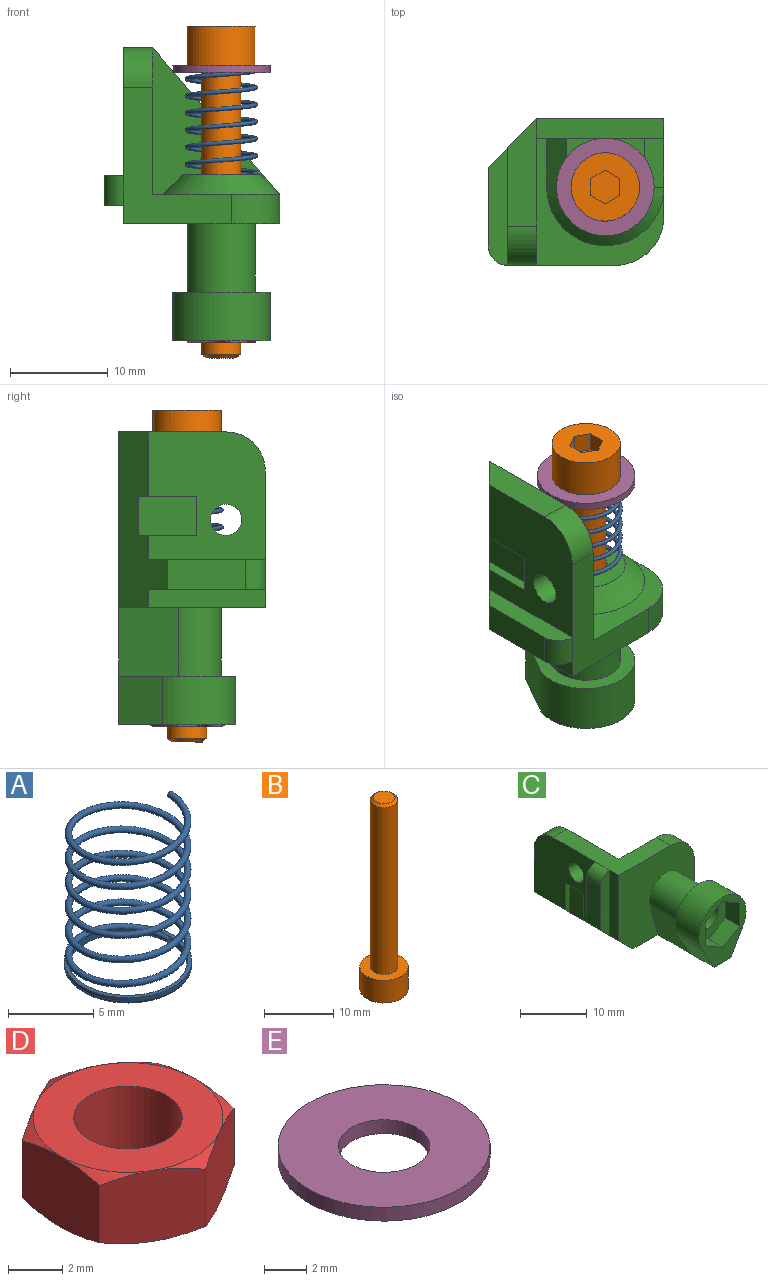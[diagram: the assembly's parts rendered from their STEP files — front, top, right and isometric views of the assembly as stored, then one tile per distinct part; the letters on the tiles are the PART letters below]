
ASSEMBLY  parts=5 mates=4
PART A: 8 faces, bbox 8.2x8.2x11.1 mm
  f0: bspline ~10.9x7.4mm, area 163.9mm2, adj f1,f2,f3,f4,f6
  f1: plane 0.46x0.26mm, normal (0,-1,0), area 0.1mm2, adj f0,f3
  f2: plane 0.46x0.46mm, normal (0,1,0), area 0.1mm2, adj f0
  f3: cylinder r=3.5mm len=7mm, axis (0,0,-1), area 9.7mm2, adj f0,f1,f4,f6,f7
  f4: cylinder r=3.5mm len=0.66mm, axis (0,0,-1), area 0mm2, adj f0,f3,f6
  f5: cylinder r=3.75mm len=7.5mm, axis (0,0,-1), area 5.9mm2, adj f6,f7
  f6: plane 7.61x7.61mm, normal (0,0,1), area 4.9mm2, adj f0,f3,f4,f5
  f7: torus R=3.5mm, axis (0,0,1), area 9mm2, adj f3,f5
PART B: 13 faces, bbox 7x7x34 mm
  f0: plane 7x7mm, normal (0,0,-1), area 30.7mm2, adj f2,f6,f7,f8,f9,f10,f11
  f1: plane 3.2x3.2mm, normal (0,0,1), area 8mm2, adj f5
  f2: cylinder r=3.5mm len=7mm, axis (0,0,-1), area 88mm2, adj f0,f3
  f3: plane 7x7mm, normal (0,0,1), area 25.9mm2, adj f2,f4
  f4: cylinder r=2mm len=29.6mm, axis (0,0,-1), area 372mm2, adj f3,f5
  f5: cone r=2mm half-angle=45deg, axis (0,0,-1), area 6.4mm2, adj f1,f4
  f6: plane 2x1.73mm, normal (-1,0,0), area 3.5mm2, adj f0,f7,f11,f12
  f7: plane 2x1.5mm, normal (-0.5,-0.87,0), area 3.5mm2, adj f0,f6,f8,f12
  f8: plane 2x1.5mm, normal (0.5,-0.87,0), area 3.5mm2, adj f0,f7,f9,f12
  f9: plane 2x1.73mm, normal (1,0,0), area 3.5mm2, adj f0,f8,f10,f12
  f10: plane 2x1.5mm, normal (0.5,0.87,0), area 3.5mm2, adj f0,f9,f11,f12
  f11: plane 2x1.5mm, normal (-0.5,0.87,0), area 3.5mm2, adj f0,f6,f10,f12
  f12: plane 3.46x3mm, normal (0,0,-1), area 7.8mm2, adj f6,f7,f8,f9,f10,f11
PART C: 43 faces, bbox 18x30x15 mm
  f0: plane 13.1x12mm, normal (-1,0,0), area 125.7mm2, adj f1,f8,f9,f16,f32,f34,f39,f40
  f1: plane 18x5mm, normal (-0.71,0,-0.71), area 79.2mm2, adj f0,f2,f3,f6,f8,f9,f10,f11
  f2: plane 8x3mm, normal (-1,0,0), area 24mm2, adj f1,f9,f10,f33
  f3: plane 30x13mm, normal (0,0,-1), area 178.5mm2, adj f1,f4,f6,f12,f13,f17,f18,f20
  f4: plane 12x10mm, normal (0,-1,0), area 44.4mm2, adj f3,f20,f21,f22,f26,f27,f28,f29
  f5: cylinder r=2.15mm len=14mm, axis (0,1,0), area 189.1mm2, adj f24,f25
  f6: plane 16x15mm, normal (0,-1,0), area 173.4mm2, adj f1,f3,f11,f12,f16,f17,f18,f19
  f7: plane 15x13mm, normal (0,0,1), area 77.5mm2, adj f13,f14,f15,f24,f36,f38
  f8: plane 11x3mm, normal (0,1,0), area 28.5mm2, adj f0,f1,f13,f14,f34
  f9: plane 12x2mm, normal (0,1,0), area 21.1mm2, adj f0,f1,f2,f33
  f10: plane 12x2mm, normal (0,-1,0), area 21.1mm2, adj f1,f2,f11,f33
  f11: plane 12x1.9mm, normal (-1,0,0), area 22.8mm2, adj f1,f6,f10,f16
  f12: plane 10x3mm, normal (1,0,0), area 30mm2, adj f3,f6,f13,f15,f35,f36
  f13: plane 15x13mm, normal (0.76,0.65,0), area 39.7mm2, adj f3,f7,f8,f12
  f14: plane 15x13mm, normal (1,0,0), area 183.5mm2, adj f7,f8,f15,f16,f32,f34
  f15: plane 13x13mm, normal (0,1,0), area 47.1mm2, adj f7,f12,f14,f16,f35,f37,f38
  f16: plane 14x11mm, normal (0,0,1), area 66mm2, adj f0,f6,f11,f14,f15,f33,f34,f35
  f17: plane 7x6.1mm, normal (-0.97,0,-0.26), area 44.2mm2, adj f3,f6,f19,f23
  f18: plane 7x6.1mm, normal (0.97,0,-0.26), area 44.2mm2, adj f3,f6,f19,f23
  f19: cylinder r=3.5mm len=7mm, axis (0,1,0), area 89.8mm2, adj f6,f17,f18,f23
  f20: plane 5x4.51mm, normal (-0.87,0,-0.5), area 26mm2, adj f3,f4,f22,f23
  f21: plane 5x4.51mm, normal (0.87,0,-0.5), area 26mm2, adj f3,f4,f22,f23
  f22: cylinder r=5mm len=10mm, axis (0,1,0), area 104.6mm2, adj f4,f20,f21,f23
  f23: plane 12x10mm, normal (0,1,0), area 33.8mm2, adj f17,f18,f19,f20,f21,f22
  f24: plane 9x8mm, normal (0,1,0), area 50.6mm2, adj f5,f7,f36,f37,f38
  f25: plane 8.43x7.3mm, normal (0,-1,0), area 31.6mm2, adj f5,f26,f27,f28,f29,f30,f31
  f26: plane 4.21x3mm, normal (-1,0,0), area 12.6mm2, adj f4,f25,f27,f31
  f27: plane 3.65x3mm, normal (-0.5,0,-0.87), area 12.6mm2, adj f4,f25,f26,f28
  f28: plane 3.65x3mm, normal (0.5,0,-0.87), area 12.6mm2, adj f4,f25,f27,f29
  f29: plane 4.21x3mm, normal (1,0,0), area 12.6mm2, adj f4,f25,f28,f30
  f30: plane 3.65x3mm, normal (0.5,0,0.87), area 12.6mm2, adj f4,f25,f29,f31
  f31: plane 3.65x3mm, normal (-0.5,0,0.87), area 12.6mm2, adj f4,f25,f26,f30
  f32: cylinder r=1.6mm len=3.2mm, axis (1,0,0), area 30.2mm2, adj f0,f14
  f33: cylinder r=2mm len=3mm, axis (0,1,0), area 9.4mm2, adj f2,f9,f10,f16
  f34: cylinder r=4mm len=4mm, axis (1,0,0), area 18.8mm2, adj f0,f8,f14,f16
  f35: cylinder r=5mm len=5mm, axis (0,-1,0), area 23.6mm2, adj f6,f12,f15,f16
  f36: plane 5x2mm, normal (0.71,0.71,0), area 14.1mm2, adj f7,f12,f24,f37
  f37: cone r=4mm half-angle=45deg, axis (0,-1,0), area 44.4mm2, adj f15,f24,f36,f38
  f38: plane 5x2mm, normal (-0.71,0.71,0), area 14.1mm2, adj f7,f15,f24,f37
  f39: plane 6x1mm, normal (0,1,0), area 5.5mm2, adj f0,f1,f41,f42
  f40: plane 6x1mm, normal (0,-1,0), area 5.5mm2, adj f0,f1,f41,f42
  f41: plane 6x4mm, normal (-1,0,0), area 24mm2, adj f1,f39,f40,f42
  f42: plane 4x1mm, normal (0,0,-1), area 4mm2, adj f0,f39,f40,f41
PART D: 21 faces, bbox 8.4x8.4x3.5 mm
  f0: plane 7x7mm, normal (0,0,1), area 25.9mm2, adj f2,f3,f4,f7,f9,f11,f13
  f1: plane 7x7mm, normal (0,0,-1), area 25.9mm2, adj f2,f5,f6,f8,f10,f12,f14
  f2: cylinder r=2mm len=4mm, axis (0,0,-1), area 40.2mm2, adj f0,f1
  f3: cone r=4.04mm half-angle=60deg, axis (0,0,-1), area 1.2mm2, adj f0,f15,f20
  f4: cone r=4.04mm half-angle=60deg, axis (0,0,-1), area 1.2mm2, adj f0,f15,f16
  f5: cone r=4.04mm half-angle=60deg, axis (0,0,1), area 1.2mm2, adj f1,f15,f20
  f6: cone r=4.04mm half-angle=60deg, axis (0,0,1), area 1.2mm2, adj f1,f15,f16
  f7: cone r=4.04mm half-angle=60deg, axis (0,0,-1), area 1.2mm2, adj f0,f16,f17
  f8: cone r=4.04mm half-angle=60deg, axis (0,0,1), area 1.2mm2, adj f1,f16,f17
  f9: cone r=4.04mm half-angle=60deg, axis (0,0,-1), area 1.2mm2, adj f0,f17,f18
  f10: cone r=4.04mm half-angle=60deg, axis (0,0,1), area 1.2mm2, adj f1,f17,f18
  f11: cone r=4.04mm half-angle=60deg, axis (0,0,-1), area 1.2mm2, adj f0,f18,f19
  f12: cone r=4.04mm half-angle=60deg, axis (0,0,1), area 1.2mm2, adj f1,f18,f19
  f13: cone r=4.04mm half-angle=60deg, axis (0,0,-1), area 1.2mm2, adj f0,f19,f20
  f14: cone r=4.04mm half-angle=60deg, axis (0,0,1), area 1.2mm2, adj f1,f19,f20
  f15: plane 3.83x3.54mm, normal (0.5,-0.87,0), area 12.1mm2, adj f3,f4,f5,f6,f16,f20
  f16: plane 3.83x3.54mm, normal (-0.5,-0.87,0), area 12.1mm2, adj f4,f6,f7,f8,f15,f17
  f17: plane 4.38x3.53mm, normal (-1,0,0), area 12.1mm2, adj f7,f8,f9,f10,f16,f18
  f18: plane 3.83x3.54mm, normal (-0.5,0.87,0), area 12.1mm2, adj f9,f10,f11,f12,f17,f19
  f19: plane 3.83x3.54mm, normal (0.5,0.87,0), area 12.1mm2, adj f11,f12,f13,f14,f18,f20
  f20: plane 4.38x3.53mm, normal (1,0,0), area 12.1mm2, adj f3,f5,f13,f14,f15,f19
PART E: 4 faces, bbox 10x10x0.8 mm
  f0: cylinder r=5mm len=10mm, axis (0,0,-1), area 25.1mm2, adj f1,f2
  f1: plane 10x10mm, normal (0,0,1), area 64mm2, adj f0,f3
  f2: plane 10x10mm, normal (0,0,-1), area 64mm2, adj f0,f3
  f3: cylinder r=2.15mm len=4.3mm, axis (0,0,-1), area 10.8mm2, adj f1,f2
PLACE A rot(axis=(-1,0,0),180deg) t=(0.06,0.01,14.13)mm
PLACE B rot(axis=(-1,0,0),180deg) t=(-80.14,9.81,18.68)mm
PLACE C rot(axis=(1,0,0),90deg) t=(-9.94,7.01,-1.57)mm fixed
PLACE D t=(-9.94,-9.99,-13.77)mm
PLACE E t=(-39.94,-19.99,13.88)mm
MATE fastened A.f3 <-> E.f0  axis (0,0,-1) through (0.06,0.01,13.88)mm
MATE slider B.f2 <-> C.f5  axis (0,0,1) through (0.06,0.01,-0.12)mm
MATE fastened D.f2 <-> C.f19  axis (0,0,1) through (0.06,0.01,-10.57)mm
MATE fastened E.f0 <-> B.f2  axis (0,0,1) through (0.06,0.01,14.68)mm
